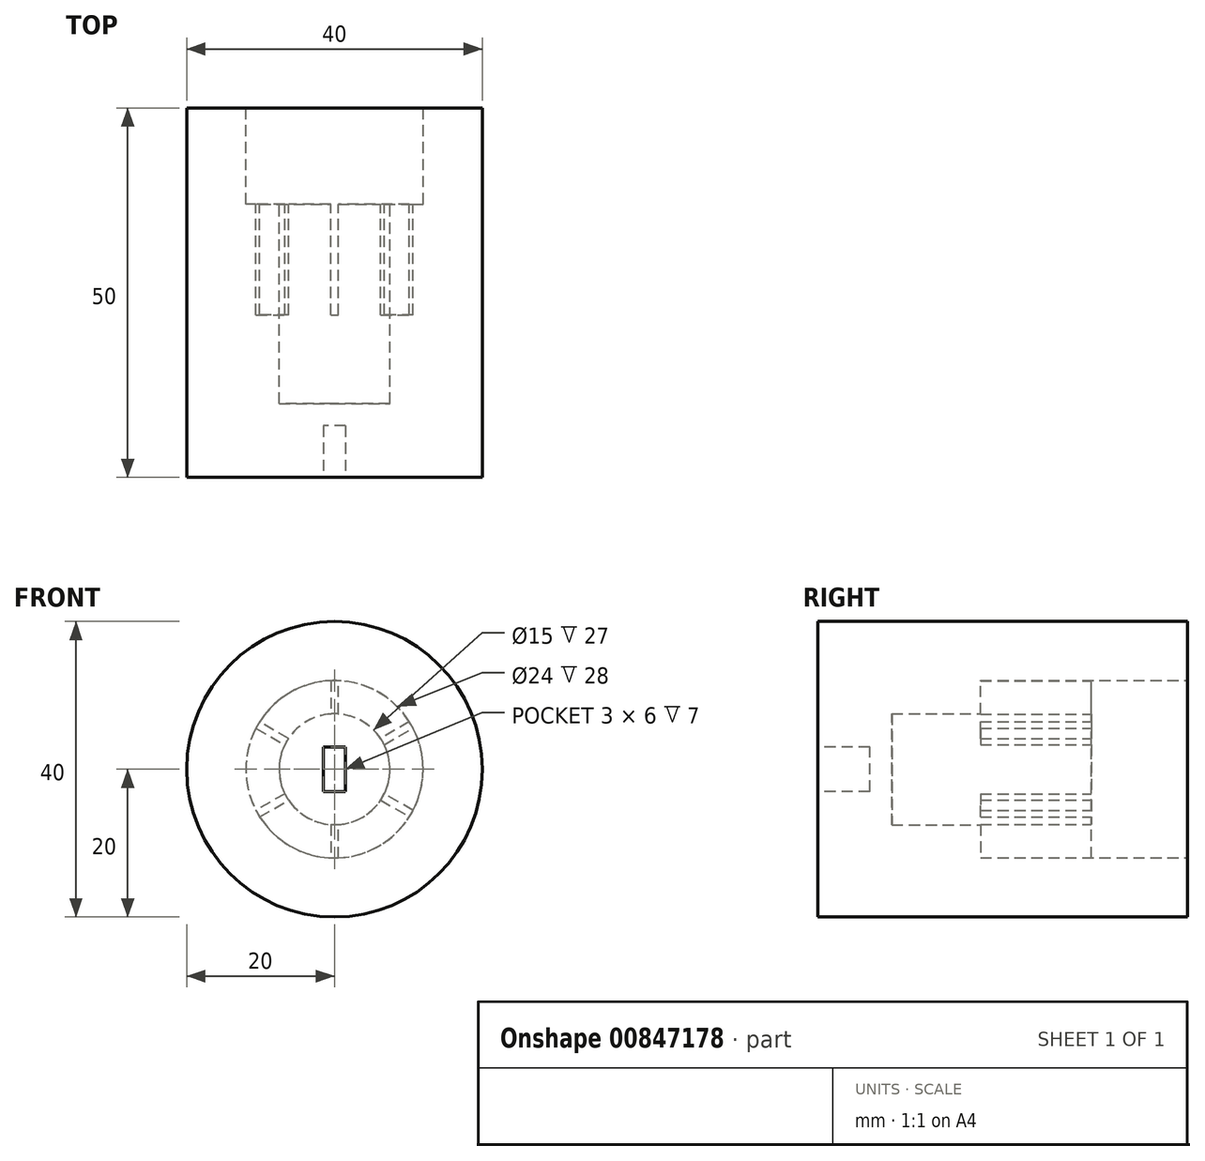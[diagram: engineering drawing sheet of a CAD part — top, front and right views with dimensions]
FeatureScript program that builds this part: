
annotation { "Feature Type Name" : "Feature", "Feature Type Description" : "" }
export const myFeature = defineFeature(function(context is Context, id is Id, definition is map)
    precondition{}
    {
        {
            var Q0;
            Q0=qCreatedBy(makeId("Front.planeOp"),FACE);
            var sketch = newSketch(context, id + "F0", { "sketchPlane" : qUnion([Q0])});
            skCircle(sketch, "E0", {"center": v(0, 0) * mm, "radius": 20 * mm});
            skCircle(sketch, "E1", {"center": v(0, 0) * mm, "radius": 12 * mm});
            skSolve(sketch);
        }
        {
            var Q0;
            Q0=makeQuery(id+"F0.imprint","IMPRINT",FACE,{"disambiguationData":[TD([[makeQuery(id+"F0.imprint","IMPRINT",EDGE,{"derivedFrom":sQuery(id+"F0.wireOp",EDGE,"E0")}),1.0]])]});
            extrude(context, id + "F1", {"entities" : qUnion([Q0]), "depth" : 50 * mm, "offsetDistance" : 25 * mm});
        }
        {
            var Q0;
            Q0=qCreatedBy(makeId("Front.planeOp"),FACE);
            cPlane(context, id + "F2", {"entities" : qUnion([Q0]), "cplaneType" : CPlaneType.OFFSET, "offset" : 13 * mm, "width" : 150 * mm, "height" : 150 * mm});
        }
        {
            var Q0;
            Q0=qCreatedBy(id+"F2.planeOp",FACE);
            var sketch = newSketch(context, id + "F3", { "sketchPlane" : qUnion([Q0])});
            skCircle(sketch, "E2", {"center": v(0, 0) * mm, "radius": 7.5 * mm});
            skCircle(sketch, "E3", {"center": v(0, 0) * mm, "radius": 12 * mm});
            skSolve(sketch);
        }
        {
            var Q0;
            Q0=makeQuery(id+"F3.imprint","IMPRINT",FACE,{"disambiguationData":[TD([[makeQuery(id+"F3.imprint","IMPRINT",EDGE,{"derivedFrom":sQuery(id+"F3.wireOp",EDGE,"E2")}),-1.0]])]});
            extrude(context, id + "F4", {"entities" : qUnion([Q0]), "operationType" : NewBodyOperationType.ADD, "depth" : (50 - 13) * mm, "offsetDistance" : 25 * mm});
        }
        {
            var Q0;
            Q0=qCreatedBy(id+"F2.planeOp",FACE);
            var sketch = newSketch(context, id + "F5", { "sketchPlane" : qUnion([Q0])});
            skLineSegment(sketch, "E4", {"start": v(0, 0) * mm, "end": v(0, 12) * mm, "construction": true});
            skLineSegment(sketch, "E5", {"start": v(-0.5, 11.99) * mm, "end": v(-0.5, 7.48) * mm});
            skLineSegment(sketch, "E6", {"start": v(0.5, 7.48) * mm, "end": v(0.5, 11.99) * mm});
            skArc(sketch, "E7", {"start": v(0.5, 11.99) * mm, "mid": v(0, 12) * mm, "end": v(-0.5, 11.99) * mm});
            skPoint(sketch, "E8.orphan", {"position": v(-0.5, 12) * mm});
            skArc(sketch, "E9", {"start": v(0.5, 7.48) * mm, "mid": v(0, 7.5) * mm, "end": v(-0.5, 7.48) * mm});
            skLineSegment(sketch, "E10.1.0", {"start": v(-6.23, 4.17) * mm, "end": v(-10.13, 6.43) * mm});
            skLineSegment(sketch, "E10.1.1", {"start": v(0, 0) * mm, "end": v(-10.4, 6) * mm, "construction": true});
            skLineSegment(sketch, "E10.1.2", {"start": v(-10.63, 5.56) * mm, "end": v(-6.73, 3.3) * mm});
            skArc(sketch, "E10.1.3", {"start": v(-6.23, 4.17) * mm, "mid": v(-6.5, 3.75) * mm, "end": v(-6.73, 3.3) * mm});
            skPoint(sketch, "E10.1.4", {"position": v(-10.64, 5.57) * mm});
            skArc(sketch, "E10.1.5", {"start": v(-10.13, 6.43) * mm, "mid": v(-10.4, 6) * mm, "end": v(-10.63, 5.56) * mm});
            skLineSegment(sketch, "E10.2.0", {"start": v(-6.73, -3.3) * mm, "end": v(-10.63, -5.56) * mm});
            skLineSegment(sketch, "E10.2.1", {"start": v(0, 0) * mm, "end": v(-10.4, -6) * mm, "construction": true});
            skLineSegment(sketch, "E10.2.2", {"start": v(-10.13, -6.43) * mm, "end": v(-6.23, -4.17) * mm});
            skArc(sketch, "E10.2.3", {"start": v(-6.73, -3.3) * mm, "mid": v(-6.5, -3.75) * mm, "end": v(-6.23, -4.17) * mm});
            skPoint(sketch, "E10.2.4", {"position": v(-10.14, -6.43) * mm});
            skArc(sketch, "E10.2.5", {"start": v(-10.63, -5.56) * mm, "mid": v(-10.4, -6) * mm, "end": v(-10.13, -6.43) * mm});
            skLineSegment(sketch, "E10.3.0", {"start": v(-0.5, -7.48) * mm, "end": v(-0.5, -11.99) * mm});
            skLineSegment(sketch, "E10.3.1", {"start": v(0, 0) * mm, "end": v(0, -12) * mm, "construction": true});
            skLineSegment(sketch, "E10.3.2", {"start": v(0.5, -11.99) * mm, "end": v(0.5, -7.48) * mm});
            skArc(sketch, "E10.3.3", {"start": v(-0.5, -7.48) * mm, "mid": v(0, -7.5) * mm, "end": v(0.5, -7.48) * mm});
            skPoint(sketch, "E10.3.4", {"position": v(0.5, -12) * mm});
            skArc(sketch, "E10.3.5", {"start": v(-0.5, -11.99) * mm, "mid": v(0, -12) * mm, "end": v(0.5, -11.99) * mm});
            skLineSegment(sketch, "E10.4.0", {"start": v(6.23, -4.17) * mm, "end": v(10.13, -6.43) * mm});
            skLineSegment(sketch, "E10.4.1", {"start": v(0, 0) * mm, "end": v(10.4, -6) * mm, "construction": true});
            skLineSegment(sketch, "E10.4.2", {"start": v(10.63, -5.56) * mm, "end": v(6.73, -3.3) * mm});
            skArc(sketch, "E10.4.3", {"start": v(6.23, -4.17) * mm, "mid": v(6.5, -3.75) * mm, "end": v(6.73, -3.3) * mm});
            skPoint(sketch, "E10.4.4", {"position": v(10.64, -5.57) * mm});
            skArc(sketch, "E10.4.5", {"start": v(10.13, -6.43) * mm, "mid": v(10.4, -6) * mm, "end": v(10.63, -5.56) * mm});
            skLineSegment(sketch, "E10.5.0", {"start": v(6.73, 3.3) * mm, "end": v(10.63, 5.56) * mm});
            skLineSegment(sketch, "E10.5.1", {"start": v(0, 0) * mm, "end": v(10.4, 6) * mm, "construction": true});
            skLineSegment(sketch, "E10.5.2", {"start": v(10.13, 6.43) * mm, "end": v(6.23, 4.17) * mm});
            skArc(sketch, "E10.5.3", {"start": v(6.73, 3.3) * mm, "mid": v(6.5, 3.75) * mm, "end": v(6.23, 4.17) * mm});
            skPoint(sketch, "E10.5.4", {"position": v(10.14, 6.43) * mm});
            skArc(sketch, "E10.5.5", {"start": v(10.63, 5.56) * mm, "mid": v(10.4, 6) * mm, "end": v(10.13, 6.43) * mm});
            skSolve(sketch);
        }
        {
            var Q0;
            Q0=makeQuery(id+"F5.imprint","IMPRINT",FACE,{"disambiguationData":[TD([[makeQuery(id+"F5.imprint","IMPRINT",EDGE,{"derivedFrom":sQuery(id+"F5.wireOp",EDGE,"E5")}),1.0]])]});
            extrude(context, id + "F6", {"entities" : qUnion([Q0]), "operationType" : NewBodyOperationType.REMOVE, "depth" : 10 * mm, "offsetDistance" : 25 * mm});
        }
        {
            var Q0;
            Q0 = qSketchRegion(id + "F5", true);
            extrude(context, id + "F7", {"entities" : qUnion([Q0]), "operationType" : NewBodyOperationType.REMOVE, "depth" : 15 * mm, "offsetDistance" : 25 * mm});
        }
        {
            var Q0;
            Q0=makeQuery(id+"F4.boolean.opBoolean","MERGE",FACE,{"derivedFrom":[makeQuery(id+"F1.opExtrude","CAP_FACE",FACE,{"disambiguationData":[OSD([sQuery(id+"F0.wireOp",EDGE,"E0"),sQuery(id+"F0.wireOp",EDGE,"E1")])],"isStart":false}),makeQuery(id+"F4.opExtrude","CAP_FACE",FACE,{"disambiguationData":[OSD([sQuery(id+"F3.wireOp",EDGE,"E2"),sQuery(id+"F3.wireOp",EDGE,"E3")])],"isStart":false})]});
            cPlane(context, id + "F8", {"entities" : qUnion([Q0]), "cplaneType" : CPlaneType.OFFSET, "offset" : 0 * mm, "width" : 150 * mm, "height" : 150 * mm});
        }
        {
            var Q0;
            Q0=qCreatedBy(id+"F8.planeOp",FACE);
            var sketch = newSketch(context, id + "F9", { "sketchPlane" : qUnion([Q0])});
            skCircle(sketch, "E11", {"center": v(0, 0) * mm, "radius": 7.5 * mm});
            skSolve(sketch);
        }
        {
            var Q0;
            Q0=makeQuery(id+"F9.imprint","IMPRINT",FACE,{"disambiguationData":[TD([[makeQuery(id+"F9.imprint","IMPRINT",EDGE,{"derivedFrom":sQuery(id+"F9.wireOp",EDGE,"E11")}),1.0]])]});
            extrude(context, id + "F10", {"entities" : qUnion([Q0]), "operationType" : NewBodyOperationType.ADD, "oppositeDirection" : true, "depth" : 10 * mm, "offsetDistance" : 25 * mm});
        }
        {
            var Q0;
            Q0=qCreatedBy(id+"F8.planeOp",FACE);
            var sketch = newSketch(context, id + "F11", { "sketchPlane" : qUnion([Q0])});
            skLineSegment(sketch, "E12", {"start": v(1.5, -3) * mm, "end": v(1.5, 3) * mm});
            skLineSegment(sketch, "E13", {"start": v(-1.5, 3) * mm, "end": v(1.5, 3) * mm});
            skLineSegment(sketch, "E14", {"start": v(-1.5, 3) * mm, "end": v(-1.5, -3) * mm});
            skLineSegment(sketch, "E15", {"start": v(1.5, -3) * mm, "end": v(-1.5, -3) * mm});
            skSolve(sketch);
        }
        {
            var Q0;
            Q0=makeQuery(id+"F11.imprint","IMPRINT",FACE,{"disambiguationData":[TD([[makeQuery(id+"F11.imprint","IMPRINT",EDGE,{"derivedFrom":sQuery(id+"F11.wireOp",EDGE,"E12")}),1.0]])]});
            extrude(context, id + "F12", {"entities" : qUnion([Q0]), "operationType" : NewBodyOperationType.REMOVE, "oppositeDirection" : true, "depth" : 7 * mm, "offsetDistance" : 25 * mm});
        }
    });
